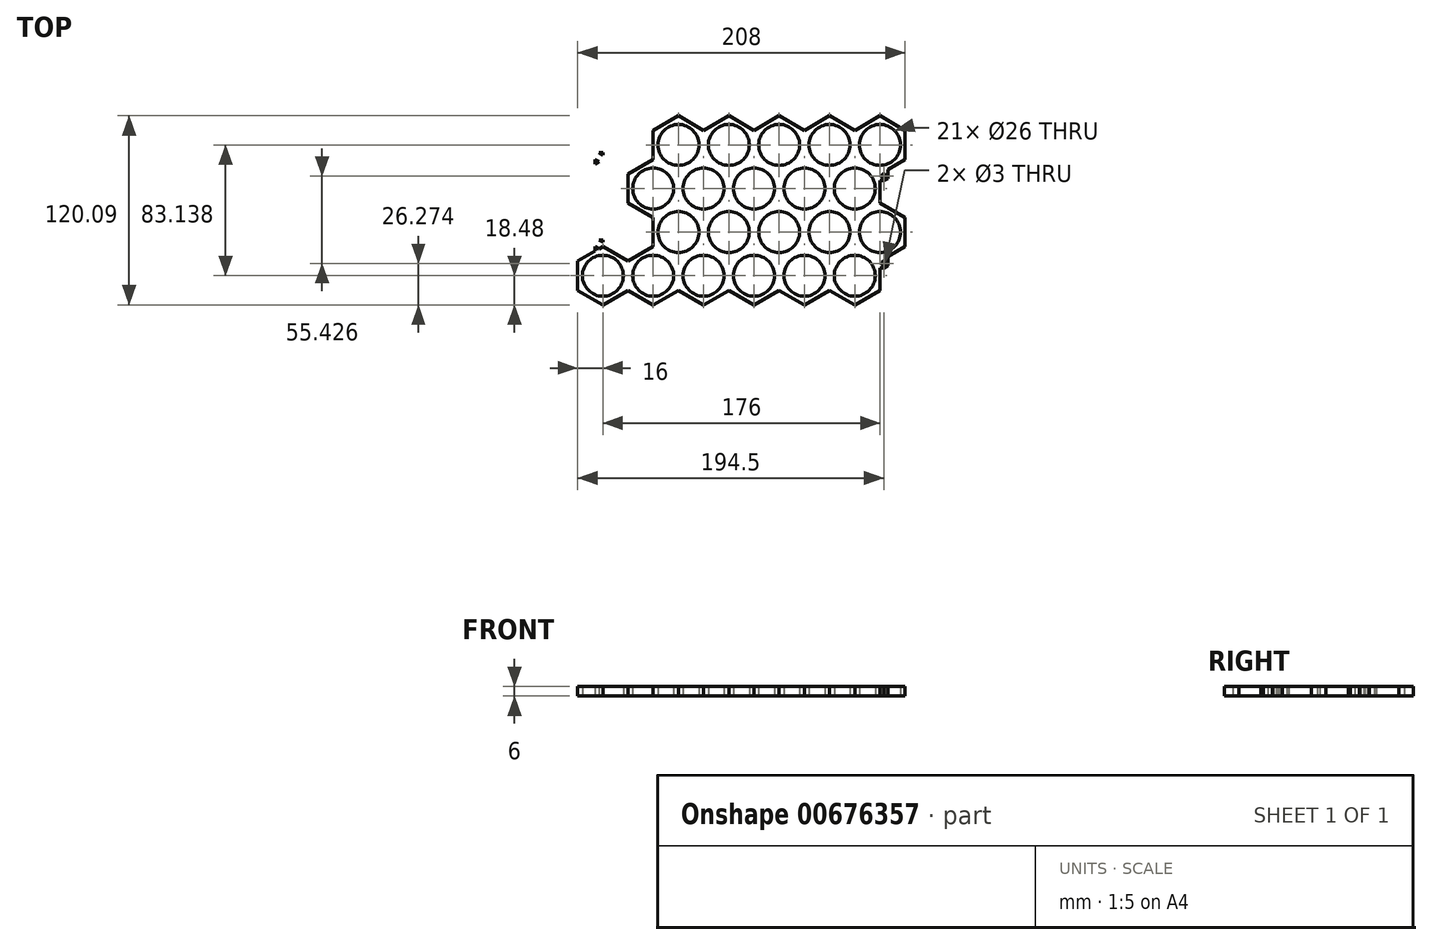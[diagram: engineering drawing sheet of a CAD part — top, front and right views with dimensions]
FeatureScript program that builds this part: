
annotation { "Feature Type Name" : "Feature", "Feature Type Description" : "" }
export const myFeature = defineFeature(function(context is Context, id is Id, definition is map)
    precondition{}
    {
        {
            var Q0;
            Q0=qCreatedBy(makeId("Top.planeOp"),FACE);
            var sketch = newSketch(context, id + "F0", { "sketchPlane" : qUnion([Q0])});
            skCircle(sketch, "E0.cCircle", {"center": v(0, 0) * mm, "radius": 16 * mm, "construction": true});
            skLineSegment(sketch, "E0.0", {"start": v(16, 9.24) * mm, "end": v(16, -9.24) * mm});
            skLineSegment(sketch, "E0.1", {"start": v(16, -9.24) * mm, "end": v(0, -18.48) * mm});
            skLineSegment(sketch, "E0.2", {"start": v(0, -18.48) * mm, "end": v(-16, -9.24) * mm});
            skLineSegment(sketch, "E0.3", {"start": v(-16, -9.24) * mm, "end": v(-16, 9.24) * mm});
            skLineSegment(sketch, "E0.4", {"start": v(-16, 9.24) * mm, "end": v(0, 18.48) * mm});
            skLineSegment(sketch, "E0.5", {"start": v(0, 18.48) * mm, "end": v(16, 9.24) * mm});
            skPoint(sketch, "E0.0.midPoint", {"position": v(16, 0) * mm});
            skLineSegment(sketch, "E1.1.0.0", {"start": v(32, 18.48) * mm, "end": v(48, 9.24) * mm});
            skLineSegment(sketch, "E1.1.0.1", {"start": v(16, 9.24) * mm, "end": v(32, 18.48) * mm});
            skLineSegment(sketch, "E1.1.0.2", {"start": v(16, -9.24) * mm, "end": v(16, 9.24) * mm});
            skLineSegment(sketch, "E1.1.0.3", {"start": v(32, -18.48) * mm, "end": v(16, -9.24) * mm});
            skLineSegment(sketch, "E1.1.0.4", {"start": v(48, -9.24) * mm, "end": v(32, -18.48) * mm});
            skLineSegment(sketch, "E1.1.0.5", {"start": v(48, 9.24) * mm, "end": v(48, -9.24) * mm});
            skLineSegment(sketch, "E1.2.0.0", {"start": v(64, 18.48) * mm, "end": v(80, 9.24) * mm});
            skLineSegment(sketch, "E1.2.0.1", {"start": v(48, 9.24) * mm, "end": v(64, 18.48) * mm});
            skLineSegment(sketch, "E1.2.0.2", {"start": v(48, -9.24) * mm, "end": v(48, 9.24) * mm});
            skLineSegment(sketch, "E1.2.0.3", {"start": v(64, -18.48) * mm, "end": v(48, -9.24) * mm});
            skLineSegment(sketch, "E1.2.0.4", {"start": v(80, -9.24) * mm, "end": v(64, -18.48) * mm});
            skLineSegment(sketch, "E1.2.0.5", {"start": v(80, 9.24) * mm, "end": v(80, -9.24) * mm});
            skLineSegment(sketch, "E1.3.0.0", {"start": v(96, 18.48) * mm, "end": v(112, 9.24) * mm});
            skLineSegment(sketch, "E1.3.0.1", {"start": v(80, 9.24) * mm, "end": v(96, 18.48) * mm});
            skLineSegment(sketch, "E1.3.0.2", {"start": v(80, -9.24) * mm, "end": v(80, 9.24) * mm});
            skLineSegment(sketch, "E1.3.0.3", {"start": v(96, -18.48) * mm, "end": v(80, -9.24) * mm});
            skLineSegment(sketch, "E1.3.0.4", {"start": v(112, -9.24) * mm, "end": v(96, -18.48) * mm});
            skLineSegment(sketch, "E1.3.0.5", {"start": v(112, 9.24) * mm, "end": v(112, -9.24) * mm});
            skLineSegment(sketch, "E1.4.0.0", {"start": v(128, 18.48) * mm, "end": v(144, 9.24) * mm});
            skLineSegment(sketch, "E1.4.0.1", {"start": v(112, 9.24) * mm, "end": v(128, 18.48) * mm});
            skLineSegment(sketch, "E1.4.0.2", {"start": v(112, -9.24) * mm, "end": v(112, 9.24) * mm});
            skLineSegment(sketch, "E1.4.0.3", {"start": v(128, -18.48) * mm, "end": v(112, -9.24) * mm});
            skLineSegment(sketch, "E1.4.0.4", {"start": v(144, -9.24) * mm, "end": v(128, -18.48) * mm});
            skLineSegment(sketch, "E1.4.0.5", {"start": v(144, 9.24) * mm, "end": v(144, -9.24) * mm});
            skLineSegment(sketch, "E1.direction1", {"start": v(0, 18.48) * mm, "end": v(32, 18.48) * mm, "construction": true});
            skCircle(sketch, "E2.cCircle", {"center": v(16, 27.71) * mm, "radius": 16 * mm, "construction": true});
            skLineSegment(sketch, "E2.0", {"start": v(32, 36.95) * mm, "end": v(32, 18.48) * mm});
            skLineSegment(sketch, "E2.1", {"start": v(32, 18.48) * mm, "end": v(16, 9.24) * mm});
            skLineSegment(sketch, "E2.2", {"start": v(16, 9.24) * mm, "end": v(0, 18.48) * mm});
            skLineSegment(sketch, "E2.3", {"start": v(0, 18.48) * mm, "end": v(0, 36.95) * mm});
            skLineSegment(sketch, "E2.4", {"start": v(0, 36.95) * mm, "end": v(16, 46.19) * mm});
            skLineSegment(sketch, "E2.5", {"start": v(16, 46.19) * mm, "end": v(32, 36.95) * mm});
            skPoint(sketch, "E2.0.midPoint", {"position": v(32, 27.71) * mm});
            skLineSegment(sketch, "E3.1.0.0", {"start": v(32, 36.95) * mm, "end": v(48, 46.19) * mm});
            skLineSegment(sketch, "E3.1.0.1", {"start": v(48, 46.19) * mm, "end": v(64, 36.95) * mm});
            skLineSegment(sketch, "E3.1.0.2", {"start": v(64, 36.95) * mm, "end": v(64, 18.48) * mm});
            skLineSegment(sketch, "E3.1.0.3", {"start": v(32, 18.48) * mm, "end": v(32, 36.95) * mm});
            skLineSegment(sketch, "E3.2.0.0", {"start": v(64, 36.95) * mm, "end": v(80, 46.19) * mm});
            skLineSegment(sketch, "E3.2.0.1", {"start": v(80, 46.19) * mm, "end": v(96, 36.95) * mm});
            skLineSegment(sketch, "E3.2.0.2", {"start": v(96, 36.95) * mm, "end": v(96, 18.48) * mm});
            skLineSegment(sketch, "E3.2.0.3", {"start": v(64, 18.48) * mm, "end": v(64, 36.95) * mm});
            skLineSegment(sketch, "E3.3.0.0", {"start": v(96, 36.95) * mm, "end": v(112, 46.19) * mm});
            skLineSegment(sketch, "E3.3.0.1", {"start": v(112, 46.19) * mm, "end": v(128, 36.95) * mm});
            skLineSegment(sketch, "E3.3.0.2", {"start": v(128, 36.95) * mm, "end": v(128, 18.48) * mm});
            skLineSegment(sketch, "E3.3.0.3", {"start": v(96, 18.48) * mm, "end": v(96, 36.95) * mm});
            skLineSegment(sketch, "E3.4.0.0", {"start": v(128, 36.95) * mm, "end": v(144, 46.19) * mm});
            skLineSegment(sketch, "E3.4.0.1", {"start": v(144, 46.19) * mm, "end": v(160, 36.95) * mm});
            skLineSegment(sketch, "E3.4.0.2", {"start": v(160, 36.95) * mm, "end": v(160, 18.48) * mm});
            skLineSegment(sketch, "E3.4.0.3", {"start": v(128, 18.48) * mm, "end": v(128, 36.95) * mm});
            skLineSegment(sketch, "E3.direction1", {"start": v(0, 36.95) * mm, "end": v(32, 36.95) * mm, "construction": true});
            skLineSegment(sketch, "E4", {"start": v(144, 9.24) * mm, "end": v(160, 18.48) * mm});
            skCircle(sketch, "E5.cCircle", {"center": v(0, 55.43) * mm, "radius": 16 * mm, "construction": true});
            skLineSegment(sketch, "E5.0", {"start": v(16, 64.66) * mm, "end": v(16, 46.19) * mm});
            skLineSegment(sketch, "E5.1", {"start": v(16, 46.19) * mm, "end": v(0, 36.95) * mm});
            skLineSegment(sketch, "E5.2", {"start": v(0, 36.95) * mm, "end": v(-16, 46.19) * mm});
            skLineSegment(sketch, "E5.3", {"start": v(-16, 46.19) * mm, "end": v(-16, 64.66) * mm});
            skLineSegment(sketch, "E5.4", {"start": v(-16, 64.66) * mm, "end": v(0, 73.9) * mm});
            skLineSegment(sketch, "E5.5", {"start": v(0, 73.9) * mm, "end": v(16, 64.66) * mm});
            skPoint(sketch, "E5.0.midPoint", {"position": v(16, 55.43) * mm});
            skLineSegment(sketch, "E6.1.0.0", {"start": v(16, 64.66) * mm, "end": v(32, 73.9) * mm});
            skLineSegment(sketch, "E6.1.0.1", {"start": v(32, 73.9) * mm, "end": v(48, 64.66) * mm});
            skLineSegment(sketch, "E6.1.0.2", {"start": v(48, 64.66) * mm, "end": v(48, 46.19) * mm});
            skLineSegment(sketch, "E6.1.0.3", {"start": v(16, 46.19) * mm, "end": v(16, 64.66) * mm});
            skLineSegment(sketch, "E6.2.0.0", {"start": v(48, 64.66) * mm, "end": v(64, 73.9) * mm});
            skLineSegment(sketch, "E6.2.0.1", {"start": v(64, 73.9) * mm, "end": v(80, 64.66) * mm});
            skLineSegment(sketch, "E6.2.0.2", {"start": v(80, 64.66) * mm, "end": v(80, 46.19) * mm});
            skLineSegment(sketch, "E6.2.0.3", {"start": v(48, 46.19) * mm, "end": v(48, 64.66) * mm});
            skLineSegment(sketch, "E6.3.0.0", {"start": v(80, 64.66) * mm, "end": v(96, 73.9) * mm});
            skLineSegment(sketch, "E6.3.0.1", {"start": v(96, 73.9) * mm, "end": v(112, 64.66) * mm});
            skLineSegment(sketch, "E6.3.0.2", {"start": v(112, 64.66) * mm, "end": v(112, 46.19) * mm});
            skLineSegment(sketch, "E6.3.0.3", {"start": v(80, 46.19) * mm, "end": v(80, 64.66) * mm});
            skLineSegment(sketch, "E6.4.0.0", {"start": v(112, 64.66) * mm, "end": v(128, 73.9) * mm});
            skLineSegment(sketch, "E6.4.0.1", {"start": v(128, 73.9) * mm, "end": v(144, 64.66) * mm});
            skLineSegment(sketch, "E6.4.0.2", {"start": v(144, 64.66) * mm, "end": v(144, 46.19) * mm});
            skLineSegment(sketch, "E6.4.0.3", {"start": v(112, 46.19) * mm, "end": v(112, 64.66) * mm});
            skLineSegment(sketch, "E6.direction1", {"start": v(-16, 64.66) * mm, "end": v(16, 64.66) * mm, "construction": true});
            skCircle(sketch, "E7.cCircle", {"center": v(16, 83.14) * mm, "radius": 16 * mm, "construction": true});
            skLineSegment(sketch, "E7.0", {"start": v(32, 92.38) * mm, "end": v(32, 73.9) * mm});
            skLineSegment(sketch, "E7.1", {"start": v(32, 73.9) * mm, "end": v(16, 64.66) * mm});
            skLineSegment(sketch, "E7.2", {"start": v(16, 64.66) * mm, "end": v(0, 73.9) * mm});
            skLineSegment(sketch, "E7.3", {"start": v(0, 73.9) * mm, "end": v(0, 92.38) * mm});
            skLineSegment(sketch, "E7.4", {"start": v(0, 92.38) * mm, "end": v(16, 101.61) * mm});
            skLineSegment(sketch, "E7.5", {"start": v(16, 101.61) * mm, "end": v(32, 92.38) * mm});
            skPoint(sketch, "E7.0.midPoint", {"position": v(32, 83.14) * mm});
            skLineSegment(sketch, "E8.1.0.0", {"start": v(32, 92.38) * mm, "end": v(48, 101.61) * mm});
            skLineSegment(sketch, "E8.1.0.1", {"start": v(48, 101.61) * mm, "end": v(64, 92.38) * mm});
            skLineSegment(sketch, "E8.1.0.2", {"start": v(32, 73.9) * mm, "end": v(32, 92.38) * mm});
            skLineSegment(sketch, "E8.1.0.3", {"start": v(64, 92.38) * mm, "end": v(64, 73.9) * mm});
            skLineSegment(sketch, "E8.2.0.0", {"start": v(64, 92.38) * mm, "end": v(80, 101.61) * mm});
            skLineSegment(sketch, "E8.2.0.1", {"start": v(80, 101.61) * mm, "end": v(96, 92.38) * mm});
            skLineSegment(sketch, "E8.2.0.2", {"start": v(64, 73.9) * mm, "end": v(64, 92.38) * mm});
            skLineSegment(sketch, "E8.2.0.3", {"start": v(96, 92.38) * mm, "end": v(96, 73.9) * mm});
            skLineSegment(sketch, "E8.3.0.0", {"start": v(96, 92.38) * mm, "end": v(112, 101.61) * mm});
            skLineSegment(sketch, "E8.3.0.1", {"start": v(112, 101.61) * mm, "end": v(128, 92.38) * mm});
            skLineSegment(sketch, "E8.3.0.2", {"start": v(96, 73.9) * mm, "end": v(96, 92.38) * mm});
            skLineSegment(sketch, "E8.3.0.3", {"start": v(128, 92.38) * mm, "end": v(128, 73.9) * mm});
            skLineSegment(sketch, "E8.4.0.0", {"start": v(128, 92.38) * mm, "end": v(144, 101.61) * mm});
            skLineSegment(sketch, "E8.4.0.1", {"start": v(144, 101.61) * mm, "end": v(160, 92.38) * mm});
            skLineSegment(sketch, "E8.4.0.2", {"start": v(128, 73.9) * mm, "end": v(128, 92.38) * mm});
            skLineSegment(sketch, "E8.4.0.3", {"start": v(160, 92.38) * mm, "end": v(160, 73.9) * mm});
            skLineSegment(sketch, "E8.direction1", {"start": v(0, 92.38) * mm, "end": v(32, 92.38) * mm, "construction": true});
            skLineSegment(sketch, "E9", {"start": v(144, 64.66) * mm, "end": v(160, 73.9) * mm});
            skCircle(sketch, "E10", {"center": v(0, 0) * mm, "radius": 13 * mm});
            skCircle(sketch, "E11", {"center": v(0, 55.43) * mm, "radius": 13 * mm});
            skCircle(sketch, "E12", {"center": v(16, 83.14) * mm, "radius": 13 * mm});
            skCircle(sketch, "E13", {"center": v(16, 27.71) * mm, "radius": 13 * mm});
            skCircle(sketch, "E14.1.0.0", {"center": v(48, 83.14) * mm, "radius": 13 * mm});
            skCircle(sketch, "E14.2.0.0", {"center": v(80, 83.14) * mm, "radius": 13 * mm});
            skCircle(sketch, "E14.3.0.0", {"center": v(112, 83.14) * mm, "radius": 13 * mm});
            skCircle(sketch, "E14.4.0.0", {"center": v(144, 83.14) * mm, "radius": 13 * mm});
            skLineSegment(sketch, "E14.direction1", {"start": v(16, 83.14) * mm, "end": v(48, 83.14) * mm, "construction": true});
            skCircle(sketch, "E15.1.0.0", {"center": v(32, 55.43) * mm, "radius": 13 * mm});
            skCircle(sketch, "E15.2.0.0", {"center": v(64, 55.43) * mm, "radius": 13 * mm});
            skCircle(sketch, "E15.3.0.0", {"center": v(96, 55.43) * mm, "radius": 13 * mm});
            skCircle(sketch, "E15.4.0.0", {"center": v(128, 55.43) * mm, "radius": 13 * mm});
            skLineSegment(sketch, "E15.direction1", {"start": v(0, 55.43) * mm, "end": v(32, 55.43) * mm, "construction": true});
            skCircle(sketch, "E16.1.0.0", {"center": v(48, 27.71) * mm, "radius": 13 * mm});
            skCircle(sketch, "E16.2.0.0", {"center": v(80, 27.71) * mm, "radius": 13 * mm});
            skCircle(sketch, "E16.3.0.0", {"center": v(112, 27.71) * mm, "radius": 13 * mm});
            skCircle(sketch, "E16.4.0.0", {"center": v(144, 27.71) * mm, "radius": 13 * mm});
            skLineSegment(sketch, "E16.direction1", {"start": v(16, 27.71) * mm, "end": v(48, 27.71) * mm, "construction": true});
            skCircle(sketch, "E17.1.0.0", {"center": v(32, 0) * mm, "radius": 13 * mm});
            skCircle(sketch, "E17.2.0.0", {"center": v(64, 0) * mm, "radius": 13 * mm});
            skCircle(sketch, "E17.3.0.0", {"center": v(96, 0) * mm, "radius": 13 * mm});
            skCircle(sketch, "E17.4.0.0", {"center": v(128, 0) * mm, "radius": 13 * mm});
            skLineSegment(sketch, "E17.direction1", {"start": v(0, 0) * mm, "end": v(32, 0) * mm, "construction": true});
            skCircle(sketch, "E18.cCircle", {"center": v(-2.5, 19.92) * mm, "radius": 2.5 * mm, "construction": true});
            skLineSegment(sketch, "E18.0", {"start": v(0, 21.36) * mm, "end": v(0, 18.48) * mm});
            skLineSegment(sketch, "E18.1", {"start": v(0, 18.48) * mm, "end": v(-2.5, 17.03) * mm});
            skLineSegment(sketch, "E18.2", {"start": v(-2.5, 17.03) * mm, "end": v(-5, 18.48) * mm});
            skLineSegment(sketch, "E18.3", {"start": v(-5, 18.48) * mm, "end": v(-5, 21.36) * mm});
            skLineSegment(sketch, "E18.4", {"start": v(-5, 21.36) * mm, "end": v(-2.5, 22.8) * mm});
            skLineSegment(sketch, "E18.5", {"start": v(-2.5, 22.8) * mm, "end": v(0, 21.36) * mm});
            skPoint(sketch, "E18.0.midPoint", {"position": v(0, 19.92) * mm});
            skCircle(sketch, "E19.cCircle", {"center": v(-2.5, 75.34) * mm, "radius": 2.5 * mm, "construction": true});
            skLineSegment(sketch, "E19.0", {"start": v(0, 76.79) * mm, "end": v(0, 73.9) * mm});
            skLineSegment(sketch, "E19.1", {"start": v(0, 73.9) * mm, "end": v(-2.5, 72.46) * mm});
            skLineSegment(sketch, "E19.2", {"start": v(-2.5, 72.46) * mm, "end": v(-5, 73.9) * mm});
            skLineSegment(sketch, "E19.3", {"start": v(-5, 73.9) * mm, "end": v(-5, 76.79) * mm});
            skLineSegment(sketch, "E19.4", {"start": v(-5, 76.79) * mm, "end": v(-2.5, 78.23) * mm});
            skLineSegment(sketch, "E19.5", {"start": v(-2.5, 78.23) * mm, "end": v(0, 76.79) * mm});
            skPoint(sketch, "E19.0.midPoint", {"position": v(0, 75.34) * mm});
            skCircle(sketch, "E20", {"center": v(-2.5, 75.34) * mm, "radius": 1.5 * mm});
            skCircle(sketch, "E21", {"center": v(-2.5, 19.92) * mm, "radius": 1.5 * mm});
            skCircle(sketch, "E22.0.5.0", {"center": v(176, 83.14) * mm, "radius": 13 * mm});
            skLineSegment(sketch, "E23.0.5.0", {"start": v(160, 92.38) * mm, "end": v(176, 101.61) * mm});
            skLineSegment(sketch, "E23.3.5.0", {"start": v(176, 101.61) * mm, "end": v(192, 92.38) * mm});
            skLineSegment(sketch, "E23.6.5.0", {"start": v(160, 73.9) * mm, "end": v(160, 92.38) * mm});
            skLineSegment(sketch, "E23.9.5.0", {"start": v(192, 92.38) * mm, "end": v(192, 73.9) * mm});
            skCircle(sketch, "E24.0.5.0", {"center": v(160, 55.43) * mm, "radius": 13 * mm});
            skCircle(sketch, "E25.0.5.0", {"center": v(160, 0) * mm, "radius": 13 * mm});
            skLineSegment(sketch, "E26.0.5.0", {"start": v(160, 18.48) * mm, "end": v(176, 9.24) * mm});
            skLineSegment(sketch, "E26.6.5.0", {"start": v(144, -9.24) * mm, "end": v(144, 9.24) * mm});
            skLineSegment(sketch, "E26.9.5.0", {"start": v(160, -18.48) * mm, "end": v(144, -9.24) * mm});
            skLineSegment(sketch, "E26.12.5.0", {"start": v(176, -9.24) * mm, "end": v(160, -18.48) * mm});
            skLineSegment(sketch, "E26.15.5.0", {"start": v(176, 9.24) * mm, "end": v(176, -9.24) * mm});
            skCircle(sketch, "E27.0.5.0", {"center": v(176, 27.71) * mm, "radius": 13 * mm});
            skLineSegment(sketch, "E28.3.5.0", {"start": v(160, 73.9) * mm, "end": v(176, 64.66) * mm});
            skLineSegment(sketch, "E28.6.5.0", {"start": v(176, 64.66) * mm, "end": v(176, 46.19) * mm});
            skLineSegment(sketch, "E28.9.5.0", {"start": v(144, 46.19) * mm, "end": v(144, 64.66) * mm});
            skLineSegment(sketch, "E29.0.5.0", {"start": v(160, 36.95) * mm, "end": v(176, 46.19) * mm});
            skLineSegment(sketch, "E29.3.5.0", {"start": v(176, 46.19) * mm, "end": v(192, 36.95) * mm});
            skLineSegment(sketch, "E29.6.5.0", {"start": v(192, 36.95) * mm, "end": v(192, 18.48) * mm});
            skLineSegment(sketch, "E29.9.5.0", {"start": v(160, 18.48) * mm, "end": v(160, 36.95) * mm});
            skLineSegment(sketch, "E30", {"start": v(192, 73.9) * mm, "end": v(176, 64.66) * mm});
            skLineSegment(sketch, "E31", {"start": v(192, 18.48) * mm, "end": v(176, 9.24) * mm});
            skCircle(sketch, "E32.cCircle", {"center": v(178.5, 63.22) * mm, "radius": 2.5 * mm, "construction": true});
            skLineSegment(sketch, "E32.0", {"start": v(181, 64.66) * mm, "end": v(181, 61.78) * mm});
            skLineSegment(sketch, "E32.1", {"start": v(181, 61.78) * mm, "end": v(178.5, 60.33) * mm});
            skLineSegment(sketch, "E32.2", {"start": v(178.5, 60.33) * mm, "end": v(176, 61.78) * mm});
            skLineSegment(sketch, "E32.3", {"start": v(176, 61.78) * mm, "end": v(176, 64.66) * mm});
            skLineSegment(sketch, "E32.4", {"start": v(176, 64.66) * mm, "end": v(178.5, 66.1) * mm});
            skLineSegment(sketch, "E32.5", {"start": v(178.5, 66.1) * mm, "end": v(181, 64.66) * mm});
            skPoint(sketch, "E32.0.midPoint", {"position": v(181, 63.22) * mm});
            skCircle(sketch, "E33", {"center": v(178.5, 63.22) * mm, "radius": 1.5 * mm});
            skCircle(sketch, "E34.cCircle", {"center": v(178.5, 7.8) * mm, "radius": 2.5 * mm, "construction": true});
            skLineSegment(sketch, "E34.0", {"start": v(181, 9.24) * mm, "end": v(181, 6.35) * mm});
            skLineSegment(sketch, "E34.1", {"start": v(181, 6.35) * mm, "end": v(178.5, 4.9) * mm});
            skLineSegment(sketch, "E34.2", {"start": v(178.5, 4.9) * mm, "end": v(176, 6.35) * mm});
            skLineSegment(sketch, "E34.3", {"start": v(176, 6.35) * mm, "end": v(176, 9.24) * mm});
            skLineSegment(sketch, "E34.4", {"start": v(176, 9.24) * mm, "end": v(178.5, 10.68) * mm});
            skLineSegment(sketch, "E34.5", {"start": v(178.5, 10.68) * mm, "end": v(181, 9.24) * mm});
            skPoint(sketch, "E34.0.midPoint", {"position": v(181, 7.8) * mm});
            skCircle(sketch, "E35", {"center": v(178.5, 7.8) * mm, "radius": 1.5 * mm});
            skLineSegment(sketch, "E36", {"start": v(181, 64.66) * mm, "end": v(181, 67.55) * mm});
            skLineSegment(sketch, "E37", {"start": v(178.5, 60.33) * mm, "end": v(176, 60.33) * mm});
            skLineSegment(sketch, "E38", {"start": v(181, 9.24) * mm, "end": v(181, 12.12) * mm});
            skLineSegment(sketch, "E39", {"start": v(178.5, 4.9) * mm, "end": v(176, 4.9) * mm});
            skLineSegment(sketch, "E40", {"start": v(-5, 73.9) * mm, "end": v(-5, 71.01) * mm});
            skLineSegment(sketch, "E41", {"start": v(-2.5, 78.23) * mm, "end": v(0, 78.23) * mm});
            skLineSegment(sketch, "E42", {"start": v(-2.5, 22.8) * mm, "end": v(0, 22.8) * mm});
            skLineSegment(sketch, "E43", {"start": v(-5, 18.48) * mm, "end": v(-5, 15.59) * mm});
            skSolve(sketch);
        }
        {
            var Q0;
            Q0=makeQuery(id+"F0.imprint","IMPRINT",FACE,{"disambiguationData":[TD([[makeQuery(id+"F0.imprint","IMPRINT",EDGE,{"derivedFrom":sQuery(id+"F0.wireOp",EDGE,"E6.2.0.1")}),1.0]])]});
            var Q1;
            Q1=makeQuery(id+"F0.imprint","IMPRINT",FACE,{"disambiguationData":[TD([[makeQuery(id+"F0.imprint","IMPRINT",EDGE,{"derivedFrom":sQuery(id+"F0.wireOp",EDGE,"E6.3.0.1")}),1.0]])]});
            var Q2;
            Q2=makeQuery(id+"F0.imprint","IMPRINT",FACE,{"disambiguationData":[TD([[makeQuery(id+"F0.imprint","IMPRINT",EDGE,{"derivedFrom":sQuery(id+"F0.wireOp",EDGE,"E6.4.0.1")}),1.0]])]});
            var Q3;
            Q3=makeQuery(id+"F0.imprint","IMPRINT",FACE,{"disambiguationData":[TD([[makeQuery(id+"F0.imprint","IMPRINT",EDGE,{"derivedFrom":sQuery(id+"F0.wireOp",EDGE,"E3.3.0.1")}),1.0]])]});
            var Q4;
            Q4=makeQuery(id+"F0.imprint","IMPRINT",FACE,{"disambiguationData":[TD([[makeQuery(id+"F0.imprint","IMPRINT",EDGE,{"derivedFrom":sQuery(id+"F0.wireOp",EDGE,"E1.4.0.0")}),1.0]])]});
            var Q5;
            Q5=makeQuery(id+"F0.imprint","IMPRINT",FACE,{"disambiguationData":[TD([[makeQuery(id+"F0.imprint","IMPRINT",EDGE,{"derivedFrom":sQuery(id+"F0.wireOp",EDGE,"E3.2.0.1")}),1.0]])]});
            var Q6;
            Q6=makeQuery(id+"F0.imprint","IMPRINT",FACE,{"disambiguationData":[TD([[makeQuery(id+"F0.imprint","IMPRINT",EDGE,{"derivedFrom":sQuery(id+"F0.wireOp",EDGE,"E1.3.0.0")}),1.0]])]});
            var Q7;
            Q7=makeQuery(id+"F0.imprint","IMPRINT",FACE,{"disambiguationData":[TD([[makeQuery(id+"F0.imprint","IMPRINT",EDGE,{"derivedFrom":sQuery(id+"F0.wireOp",EDGE,"E1.4.0.0")}),-1.0]])]});
            var Q8;
            Q8=makeQuery(id+"F0.imprint","IMPRINT",FACE,{"disambiguationData":[TD([[makeQuery(id+"F0.imprint","IMPRINT",EDGE,{"derivedFrom":sQuery(id+"F0.wireOp",EDGE,"E1.3.0.0")}),-1.0]])]});
            var Q9;
            Q9=makeQuery(id+"F0.imprint","IMPRINT",FACE,{"disambiguationData":[TD([[makeQuery(id+"F0.imprint","IMPRINT",EDGE,{"derivedFrom":sQuery(id+"F0.wireOp",EDGE,"E3.1.0.1")}),1.0]])]});
            var Q10;
            Q10=makeQuery(id+"F0.imprint","IMPRINT",FACE,{"disambiguationData":[TD([[makeQuery(id+"F0.imprint","IMPRINT",EDGE,{"derivedFrom":sQuery(id+"F0.wireOp",EDGE,"E1.2.0.0")}),1.0]])]});
            var Q11;
            Q11=makeQuery(id+"F0.imprint","IMPRINT",FACE,{"disambiguationData":[TD([[makeQuery(id+"F0.imprint","IMPRINT",EDGE,{"derivedFrom":sQuery(id+"F0.wireOp",EDGE,"E6.1.0.1")}),1.0]])]});
            var Q12;
            Q12=makeQuery(id+"F0.imprint","IMPRINT",FACE,{"disambiguationData":[TD([[makeQuery(id+"F0.imprint","IMPRINT",EDGE,{"derivedFrom":sQuery(id+"F0.wireOp",EDGE,"E7.1")}),-1.0]])]});
            var Q13;
            Q13=makeQuery(id+"F0.imprint","IMPRINT",FACE,{"disambiguationData":[TD([[makeQuery(id+"F0.imprint","IMPRINT",EDGE,{"derivedFrom":sQuery(id+"F0.wireOp",EDGE,"E2.5")}),1.0]])]});
            var Q14;
            Q14=makeQuery(id+"F0.imprint","IMPRINT",FACE,{"disambiguationData":[TD([[makeQuery(id+"F0.imprint","IMPRINT",EDGE,{"derivedFrom":sQuery(id+"F0.wireOp",EDGE,"E1.1.0.0")}),1.0]])]});
            var Q15;
            Q15=makeQuery(id+"F0.imprint","IMPRINT",FACE,{"disambiguationData":[TD([[makeQuery(id+"F0.imprint","IMPRINT",EDGE,{"derivedFrom":sQuery(id+"F0.wireOp",EDGE,"E5.1")}),-1.0]])]});
            var Q16;
            Q16=makeQuery(id+"F0.imprint","IMPRINT",FACE,{"disambiguationData":[TD([[makeQuery(id+"F0.imprint","IMPRINT",EDGE,{"derivedFrom":sQuery(id+"F0.wireOp",EDGE,"E2.1")}),-1.0]])]});
            var Q17;
            Q17=makeQuery(id+"F0.imprint","IMPRINT",FACE,{"disambiguationData":[TD([[makeQuery(id+"F0.imprint","IMPRINT",EDGE,{"derivedFrom":sQuery(id+"F0.wireOp",EDGE,"E1.1.0.0")}),-1.0]])]});
            var Q18;
            Q18=makeQuery(id+"F0.imprint","IMPRINT",FACE,{"disambiguationData":[TD([[makeQuery(id+"F0.imprint","IMPRINT",EDGE,{"derivedFrom":sQuery(id+"F0.wireOp",EDGE,"E1.2.0.0")}),-1.0]])]});
            var Q19;
            Q19=makeQuery(id+"F0.imprint","IMPRINT",FACE,{"disambiguationData":[TD([[makeQuery(id+"F0.imprint","IMPRINT",EDGE,{"derivedFrom":sQuery(id+"F0.wireOp",EDGE,"E0.1")}),-1.0]])]});
            var Q20;
            Q20=makeQuery(id+"F0.imprint","IMPRINT",FACE,{"disambiguationData":[TD([[makeQuery(id+"F0.imprint","IMPRINT",EDGE,{"derivedFrom":sQuery(id+"F0.wireOp",EDGE,"E3.4.0.1")}),1.0]])]});
            var Q21;
            Q21=makeQuery(id+"F0.imprint","IMPRINT",FACE,{"disambiguationData":[TD([[makeQuery(id+"F0.imprint","IMPRINT",EDGE,{"derivedFrom":sQuery(id+"F0.wireOp",EDGE,"E22.0.5.0")}),-1.0]])]});
            var Q22;
            Q22=makeQuery(id+"F0.imprint","IMPRINT",FACE,{"disambiguationData":[TD([[makeQuery(id+"F0.imprint","IMPRINT",EDGE,{"derivedFrom":sQuery(id+"F0.wireOp",EDGE,"E26.0.5.0")}),1.0]])]});
            var Q23;
            Q23=makeQuery(id+"F0.imprint","IMPRINT",FACE,{"disambiguationData":[TD([[makeQuery(id+"F0.imprint","IMPRINT",EDGE,{"derivedFrom":sQuery(id+"F0.wireOp",EDGE,"E25.0.5.0")}),-1.0]])]});
            extrude(context, id + "F1", {"entities" : qUnion([Q0, Q1, Q2, Q3, Q4, Q5, Q6, Q7, Q8, Q9, Q10, Q11, Q12, Q13, Q14, Q15, Q16, Q17, Q18, Q19, Q20, Q21, Q22, Q23]), "depth" : 6 * mm, "offsetDistance" : 25 * mm});
        }
        {
            var Q0;
            Q0=makeQuery(id+"F0.imprint","IMPRINT",FACE,{"disambiguationData":[TD([[makeQuery(id+"F0.imprint","IMPRINT",EDGE,{"derivedFrom":sQuery(id+"F0.wireOp",EDGE,"e7853617-d38c-451f-b675-df6a1fb21218.0")}),-1.0]])]});
            var Q1;
            Q1=makeQuery(id+"F0.imprint","IMPRINT",FACE,{"disambiguationData":[TD([[makeQuery(id+"F0.imprint","IMPRINT",EDGE,{"derivedFrom":sQuery(id+"F0.wireOp",EDGE,"500f74cc-9e8b-4941-b389-d23673d83a33.0")}),-1.0]])]});
            var Q2;
            Q2=makeQuery(id+"F0.imprint","IMPRINT",FACE,{"disambiguationData":[TD([[makeQuery(id+"F0.imprint","IMPRINT",EDGE,{"derivedFrom":sQuery(id+"F0.wireOp",EDGE,"E18.0")}),-1.0]])]});
            var Q3;
            Q3=makeQuery(id+"F0.imprint","IMPRINT",FACE,{"disambiguationData":[TD([[makeQuery(id+"F0.imprint","IMPRINT",EDGE,{"derivedFrom":sQuery(id+"F0.wireOp",EDGE,"E19.0")}),-1.0]])]});
            var Q4;
            Q4=makeQuery(id+"F0.imprint","IMPRINT",FACE,{"disambiguationData":[TD([[makeQuery(id+"F0.imprint","IMPRINT",EDGE,{"derivedFrom":sQuery(id+"F0.wireOp",EDGE,"E34.0")}),-1.0]])]});
            var Q5;
            Q5=makeQuery(id+"F0.imprint","IMPRINT",FACE,{"disambiguationData":[TD([[makeQuery(id+"F0.imprint","IMPRINT",EDGE,{"derivedFrom":sQuery(id+"F0.wireOp",EDGE,"E32.0")}),-1.0]])]});
            var Q6;
            {var subQ0=sQuery(id+"F0.wireOp",EDGE,"E19.2");Q6=makeQuery(id+"F0.imprint","IMPRINT",FACE,{"disambiguationData":[TD([[makeQuery(id+"F0.imprint","IMPRINT",EDGE,{"derivedFrom":subQ0}),1.0]])]});}
            var Q7;
            {var subQ0=sQuery(id+"F0.wireOp",EDGE,"E19.5");Q7=makeQuery(id+"F0.imprint","IMPRINT",FACE,{"disambiguationData":[TD([[makeQuery(id+"F0.imprint","IMPRINT",EDGE,{"derivedFrom":subQ0}),1.0]])]});}
            var Q8;
            {var subQ0=sQuery(id+"F0.wireOp",EDGE,"E18.5");Q8=makeQuery(id+"F0.imprint","IMPRINT",FACE,{"disambiguationData":[TD([[makeQuery(id+"F0.imprint","IMPRINT",EDGE,{"derivedFrom":subQ0}),1.0]])]});}
            var Q9;
            {var subQ0=sQuery(id+"F0.wireOp",EDGE,"E18.2");Q9=makeQuery(id+"F0.imprint","IMPRINT",FACE,{"disambiguationData":[TD([[makeQuery(id+"F0.imprint","IMPRINT",EDGE,{"derivedFrom":subQ0}),1.0]])]});}
            var Q10;
            {var subQ0=sQuery(id+"F0.wireOp",EDGE,"E32.2");Q10=makeQuery(id+"F0.imprint","IMPRINT",FACE,{"disambiguationData":[TD([[makeQuery(id+"F0.imprint","IMPRINT",EDGE,{"derivedFrom":subQ0}),1.0]])]});}
            var Q11;
            {var subQ0=sQuery(id+"F0.wireOp",EDGE,"E32.5");Q11=makeQuery(id+"F0.imprint","IMPRINT",FACE,{"disambiguationData":[TD([[makeQuery(id+"F0.imprint","IMPRINT",EDGE,{"derivedFrom":subQ0}),1.0]])]});}
            var Q12;
            {var subQ0=sQuery(id+"F0.wireOp",EDGE,"E34.2");Q12=makeQuery(id+"F0.imprint","IMPRINT",FACE,{"disambiguationData":[TD([[makeQuery(id+"F0.imprint","IMPRINT",EDGE,{"derivedFrom":subQ0}),1.0]])]});}
            var Q13;
            {var subQ0=sQuery(id+"F0.wireOp",EDGE,"E34.5");Q13=makeQuery(id+"F0.imprint","IMPRINT",FACE,{"disambiguationData":[TD([[makeQuery(id+"F0.imprint","IMPRINT",EDGE,{"derivedFrom":subQ0}),1.0]])]});}
            extrude(context, id + "F2", {"entities" : qUnion([Q0, Q1, Q2, Q3, Q4, Q5, Q6, Q7, Q8, Q9, Q10, Q11, Q12, Q13]), "operationType" : NewBodyOperationType.ADD, "depth" : 6 * mm, "offsetDistance" : 25 * mm});
        }
    });
